# Revit family: Safety & Protection_Barrier_UltiGroup_Dok Guardian
name_source: partatom
category: Specialty Equipment
revit_build: Autodesk Revit Architecture 2016 (Build: 20150220_1215(x64)
units: mm (PartAtom-declared; Revit-internal decimal feet)

## family parameters
Cut with Voids When Loaded = No
Host = Face
OmniClass Number = 23.50.70.00
OmniClass Title = Loading Dock Equipment
Part Type = Normal
Room Calculation Point = No
Round Connector Dimension = Use Diameter
Shared = No

## types (2) — shared parameters
Fax = 17 McKee Street, Te Rapa, Hamilton, 3200, New Zealand
Left Guard Width = 406 mm
Manufacturer = UltiGroup
Maximum Clear Opening Width = 5004 mm
Send Message = http://ultigroup.co.nz
zero-valued in all types: Default Elevation, Expected Lifespan (Years), InstallationGroup_ANZRS, Maintenance Schedule (Months), ModifiedIssue_ANZRS, Warranty Duration (Years)

## per-type parameters (varying)
| type | Capacity | Description | HD | LD | Left Guard Depth | Model | Right Guard Depth | Right Guard Width | URL |
| Light Duty | 454 kilograms at 4 MPH | Loading Dock Safety Barrier - Dok-Guardian LD Safety Barrier as Specified | No | Yes | 279 mm | Dok-Guardian LD Safety Barrier | 273 mm | 400 mm |  |
| Heavy Duty | 4540 kilograms at 4 MPH | Loading Dock Safety Barrier - Dok-Guardian Safety Barrier as Specified | Yes | No | 394 mm | Dok-Guardian Safety Barrier | 343 mm | 406 mm | www.ultigroup.co.nz |

## geometry (parser evidence)
native form markers: Blend x8, Sweep x5
no freeform markers — native parametric forms only
